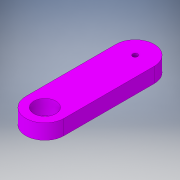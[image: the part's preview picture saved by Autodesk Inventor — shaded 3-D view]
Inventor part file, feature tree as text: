
AUTODESK INVENTOR PART (.ipt)
format: ipt  version: 2017 (Build 210142000, 142)  size: 117,248 bytes
history: native  units: in
note: dims shown in document units (in); Inventor stores cm internally (conversion verified against a paired STEP export)
features: extrude x1, sketch x1
ambient origin geometry x8: Origin, YZ Plane, XZ Plane, XY Plane, X Axis, Y Axis, Z Axis, Center Point
bodies: Solid1 (feature_tree)
feature tree (2):
  extrude  "Extrusion1"  Depth=0.748in
  sketch  "Sketch1"  dims[d0=1.4961in d2=0.748in d3=0.8661in d4=0.1969in d6=0.0in]
